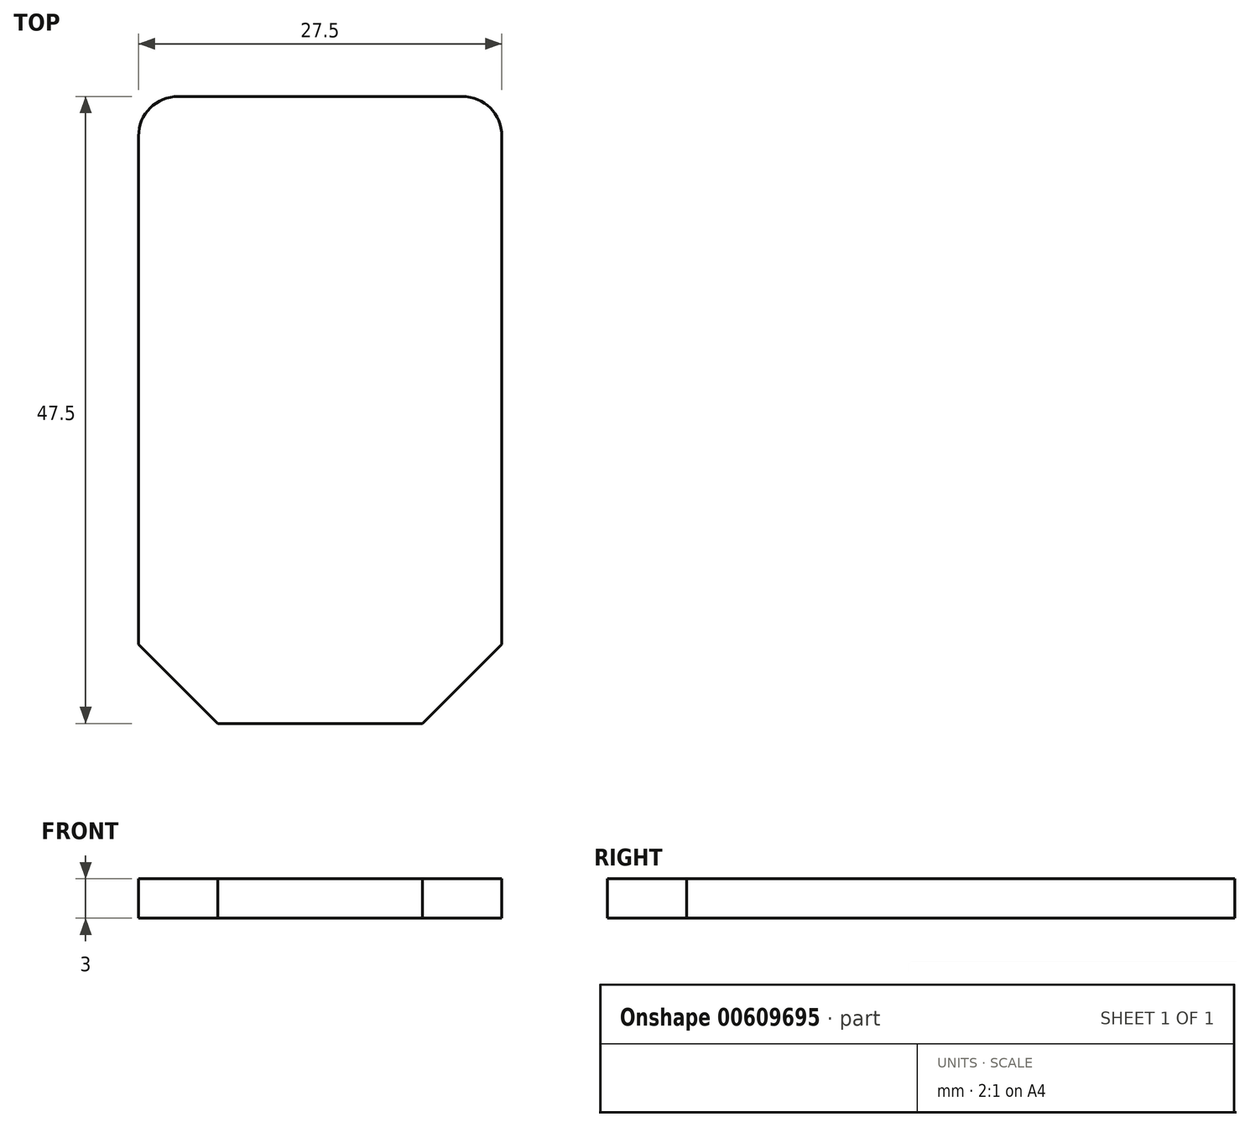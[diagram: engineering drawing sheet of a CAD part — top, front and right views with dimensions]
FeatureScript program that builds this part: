
annotation { "Feature Type Name" : "Feature", "Feature Type Description" : "" }
export const myFeature = defineFeature(function(context is Context, id is Id, definition is map)
    precondition{}
    {
        {
            var Q0;
            Q0=qCreatedBy(makeId("Top.planeOp"),FACE);
            var sketch = newSketch(context, id + "F0", { "sketchPlane" : qUnion([Q0])});
            skLineSegment(sketch, "E0", {"start": v(-67.69, 45.22) * mm, "end": v(-46.19, 45.22) * mm});
            skLineSegment(sketch, "E1", {"start": v(-43.19, 42.22) * mm, "end": v(-43.19, 3.72) * mm});
            skLineSegment(sketch, "E2", {"start": v(-49.19, -2.28) * mm, "end": v(-64.69, -2.28) * mm});
            skLineSegment(sketch, "E3", {"start": v(-70.69, 3.72) * mm, "end": v(-70.69, 42.22) * mm});
            skLineSegment(sketch, "E4", {"start": v(-64.69, -2.28) * mm, "end": v(-70.69, 3.72) * mm});
            skLineSegment(sketch, "E5", {"start": v(-43.19, 3.72) * mm, "end": v(-49.19, -2.28) * mm});
            skPoint(sketch, "E6.orphan", {"position": v(-70.69, -2.28) * mm});
            skPoint(sketch, "E7.visualSharp", {"position": v(-70.69, 45.22) * mm});
            skArc(sketch, "E7.filletArc", {"start": v(-67.69, 45.22) * mm, "mid": v(-69.8, 44.34) * mm, "end": v(-70.69, 42.22) * mm});
            skPoint(sketch, "E8.visualSharp", {"position": v(-43.19, 45.22) * mm});
            skArc(sketch, "E8.filletArc", {"start": v(-43.19, 42.22) * mm, "mid": v(-44.06, 44.34) * mm, "end": v(-46.19, 45.22) * mm});
            skSolve(sketch);
        }
        {
            var Q0;
            Q0=makeQuery(id+"F0.imprint","IMPRINT",FACE,{"disambiguationData":[TD([[makeQuery(id+"F0.imprint","IMPRINT",EDGE,{"derivedFrom":sQuery(id+"F0.wireOp",EDGE,"E0")}),-1.0]])]});
            extrude(context, id + "F1", {"entities" : qUnion([Q0]), "depth" : 3 * mm, "offsetDistance" : 25 * mm});
        }
    });
